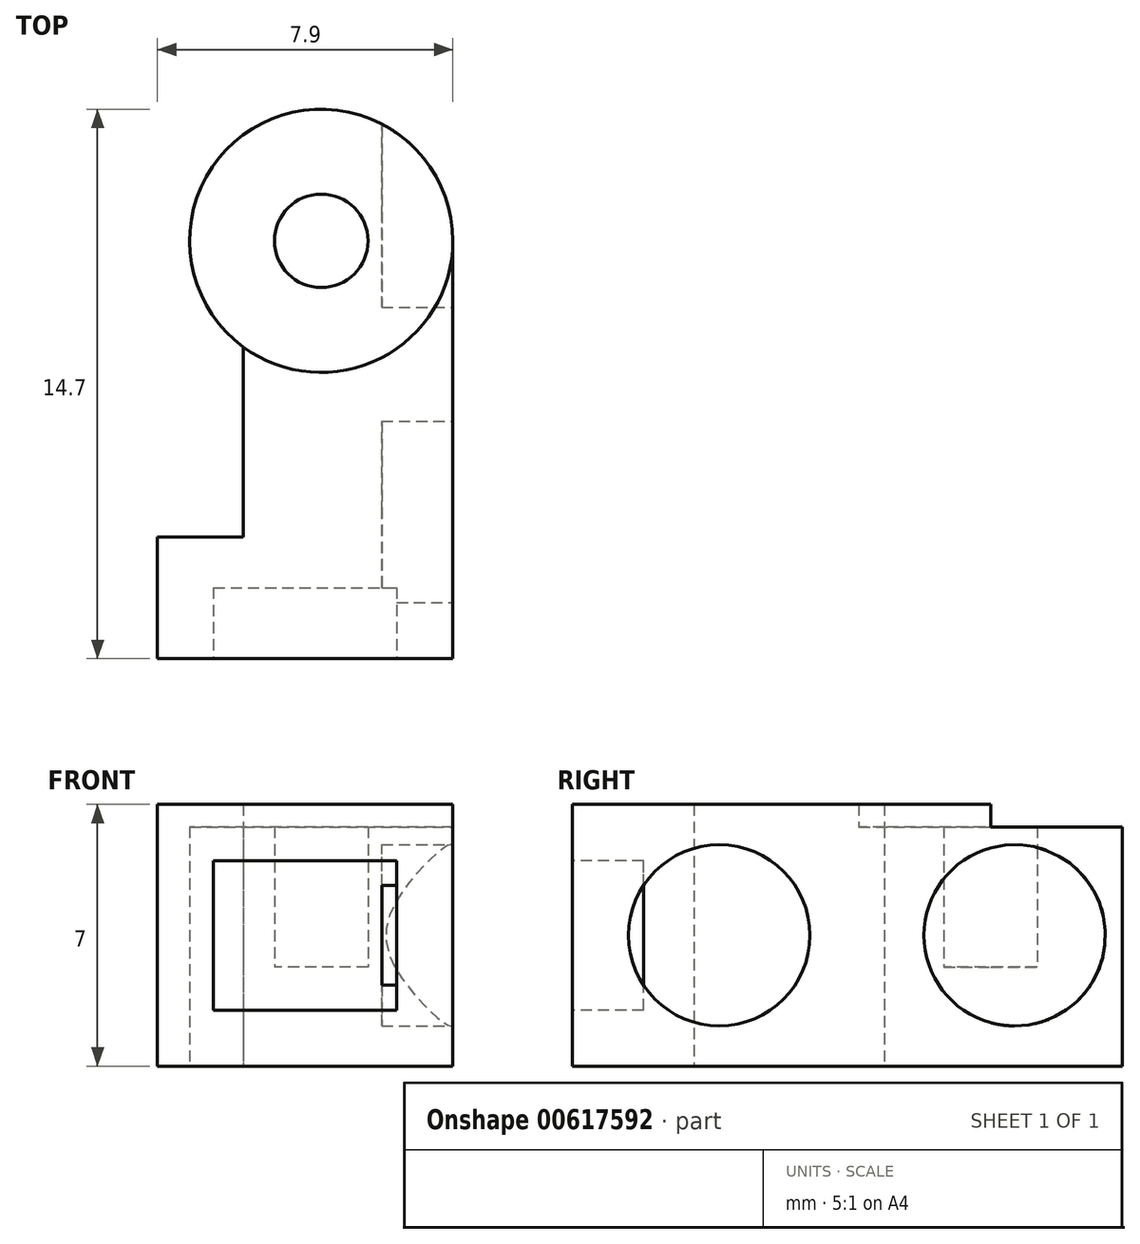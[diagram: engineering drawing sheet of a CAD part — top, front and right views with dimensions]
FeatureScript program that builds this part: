
annotation { "Feature Type Name" : "Feature", "Feature Type Description" : "" }
export const myFeature = defineFeature(function(context is Context, id is Id, definition is map)
    precondition{}
    {
        {
            var Q0;
            Q0=qCreatedBy(makeId("Top.planeOp"),FACE);
            var sketch = newSketch(context, id + "F0", { "sketchPlane" : qUnion([Q0])});
            skCircle(sketch, "E0", {"center": v(0, 0) * mm, "radius": 3.52 * mm});
            skLineSegment(sketch, "E1", {"start": v(0, 3.52) * mm, "end": v(0, -11.18) * mm, "construction": true});
            skLineSegment(sketch, "E2", {"start": v(0, -11.18) * mm, "end": v(3.52, -11.18) * mm});
            skLineSegment(sketch, "E3", {"start": v(3.52, -11.18) * mm, "end": v(3.52, 0) * mm});
            skLineSegment(sketch, "E4", {"start": v(0, -11.18) * mm, "end": v(-4.38, -11.18) * mm});
            skLineSegment(sketch, "E5", {"start": v(-4.38, -11.18) * mm, "end": v(-4.38, -7.93) * mm});
            skLineSegment(sketch, "E6", {"start": v(-4.38, -7.93) * mm, "end": v(-2.08, -7.93) * mm});
            skLineSegment(sketch, "E7", {"start": v(-2.08, -7.93) * mm, "end": v(-2.08, -2.84) * mm});
            skCircle(sketch, "E8", {"center": v(0, 0) * mm, "radius": 1.25 * mm});
            skSolve(sketch);
        }
        {
            var Q0;
            Q0=makeQuery(id+"F0.imprint","IMPRINT",FACE,{"disambiguationData":[TD([[makeQuery(id+"F0.imprint","IMPRINT",EDGE,{"derivedFrom":sQuery(id+"F0.wireOp",EDGE,"E2")}),1.0]])]});
            extrude(context, id + "F1", {"entities" : qUnion([Q0]), "depth" : 7 * mm, "offsetDistance" : 25 * mm});
        }
        {
            var Q0;
            Q0=makeQuery(id+"F0.imprint","IMPRINT",FACE,{"disambiguationData":[TD([[makeQuery(id+"F0.imprint","IMPRINT",EDGE,{"derivedFrom":sQuery(id+"F0.wireOp",EDGE,"E8")}),-1.0]])]});
            extrude(context, id + "F2", {"entities" : qUnion([Q0]), "operationType" : NewBodyOperationType.ADD, "depth" : 6.4 * mm, "offsetDistance" : 25 * mm});
        }
        {
            var Q0;
            Q0=makeQuery(id+"F0.imprint","IMPRINT",FACE,{"disambiguationData":[TD([[makeQuery(id+"F0.imprint","IMPRINT",EDGE,{"derivedFrom":sQuery(id+"F0.wireOp",EDGE,"E8")}),1.0]])]});
            extrude(context, id + "F3", {"entities" : qUnion([Q0]), "operationType" : NewBodyOperationType.ADD, "depth" : 2.65 * mm, "offsetDistance" : 25 * mm});
        }
        {
            var Q0;
            Q0=makeQuery(id+"F1.opExtrude","SWEPT_FACE",FACE,{"disambiguationData":[OSD([sQuery(id+"F0.wireOp",EDGE,"E2"),sQuery(id+"F0.wireOp",EDGE,"E4")])]});
            var sketch = newSketch(context, id + "F4", { "sketchPlane" : qUnion([Q0])});
            skLineSegment(sketch, "E9.bottom", {"start": v(-4.38, 0) * mm, "end": v(3.52, 0) * mm});
            skLineSegment(sketch, "E9.top", {"start": v(-4.38, 7) * mm, "end": v(3.52, 7) * mm});
            skLineSegment(sketch, "E9.left", {"start": v(-4.38, 0) * mm, "end": v(-4.38, 7) * mm});
            skLineSegment(sketch, "E9.right", {"start": v(3.52, 0) * mm, "end": v(3.52, 7) * mm});
            skLineSegment(sketch, "E10.0", {"start": v(-2.88, 1.5) * mm, "end": v(-2.88, 5.5) * mm});
            skLineSegment(sketch, "E10.1", {"start": v(-2.88, 1.5) * mm, "end": v(2.02, 1.5) * mm});
            skLineSegment(sketch, "E10.2", {"start": v(2.02, 1.5) * mm, "end": v(2.02, 5.5) * mm});
            skLineSegment(sketch, "E10.3", {"start": v(-2.88, 5.5) * mm, "end": v(2.02, 5.5) * mm});
            skSolve(sketch);
        }
        {
            var Q0;
            Q0=makeQuery(id+"F4.imprint","IMPRINT",FACE,{"disambiguationData":[TD([[makeQuery(id+"F4.imprint","IMPRINT",EDGE,{"derivedFrom":sQuery(id+"F4.wireOp",EDGE,"E10.0")}),-1.0]])]});
            extrude(context, id + "F5", {"entities" : qUnion([Q0]), "operationType" : NewBodyOperationType.REMOVE, "oppositeDirection" : true, "depth" : 1.9 * mm, "offsetDistance" : 25 * mm});
        }
        {
            var Q0;
            Q0=makeQuery(id+"F1.opExtrude","SWEPT_FACE",FACE,{"disambiguationData":[OSD([sQuery(id+"F0.wireOp",EDGE,"E3")])]});
            var sketch = newSketch(context, id + "F6", { "sketchPlane" : qUnion([Q0])});
            skLineSegment(sketch, "E11.bottom", {"start": v(-11.18, 0) * mm, "end": v(3.52, 0) * mm});
            skLineSegment(sketch, "E11.top", {"start": v(-11.18, 7) * mm, "end": v(3.52, 7) * mm});
            skLineSegment(sketch, "E11.left", {"start": v(-11.18, 0) * mm, "end": v(-11.18, 7) * mm});
            skLineSegment(sketch, "E11.right", {"start": v(3.52, 0) * mm, "end": v(3.52, 7) * mm});
            skLineSegment(sketch, "E12", {"start": v(-11.18, 3.5) * mm, "end": v(3.52, 3.5) * mm, "construction": true});
            skCircle(sketch, "E13", {"center": v(-7.25, 3.5) * mm, "radius": 2.43 * mm});
            skCircle(sketch, "E14", {"center": v(0.65, 3.5) * mm, "radius": 2.43 * mm});
            skSolve(sketch);
        }
        {
            var Q0;
            Q0=makeQuery(id+"F6.imprint","IMPRINT",FACE,{"disambiguationData":[TD([[makeQuery(id+"F6.imprint","IMPRINT",EDGE,{"derivedFrom":sQuery(id+"F6.wireOp",EDGE,"E13")}),1.0]])]});
            var Q1;
            {var subQ0=sQuery(id+"F6.wireOp",EDGE,"E14");var subQ1=sQuery(id+"F0.wireOp",EDGE,"E3");var subQ2=sQuery(id+"F0.wireOp",EDGE,"E0");var subQ3=makeQuery(id+"F2.boolean.opBoolean","SPLIT",EDGE,{"disambiguationData":[topologyDisambiguationEdgeConnected([makeQuery(id+"F2.opExtrude","SWEPT_FACE",FACE,{"disambiguationData":[OSD([subQ2])]})])],"derivedFrom":makeQuery(id+"F1.opExtrude","SWEPT_EDGE",EDGE,{"disambiguationData":[OSD([subQ2,subQ1])]})});var subQ4=makeQuery(id+"F6.imprint","INTERSECT",VERTEX,{"disambiguationData":[OD(0.0)],"derivedFrom":[subQ3,subQ0]});Q1=makeQuery(id+"F6.imprint","IMPRINT",FACE,{"disambiguationData":[TD([[makeQuery(id+"F6.imprint","IMPRINT",EDGE,{"disambiguationData":[TD([[subQ4,1.0]])],"derivedFrom":subQ0}),1.0]])]});}
            var Q2;
            {var subQ0=sQuery(id+"F6.wireOp",EDGE,"E14");var subQ1=sQuery(id+"F0.wireOp",EDGE,"E3");var subQ2=sQuery(id+"F0.wireOp",EDGE,"E0");var subQ3=makeQuery(id+"F2.boolean.opBoolean","SPLIT",EDGE,{"disambiguationData":[topologyDisambiguationEdgeConnected([makeQuery(id+"F2.opExtrude","SWEPT_FACE",FACE,{"disambiguationData":[OSD([subQ2])]})])],"derivedFrom":makeQuery(id+"F1.opExtrude","SWEPT_EDGE",EDGE,{"disambiguationData":[OSD([subQ2,subQ1])]})});var subQ4=makeQuery(id+"F6.imprint","INTERSECT",VERTEX,{"disambiguationData":[OD(0.0)],"derivedFrom":[subQ3,subQ0]});Q2=makeQuery(id+"F6.imprint","IMPRINT",FACE,{"disambiguationData":[TD([[makeQuery(id+"F6.imprint","IMPRINT",EDGE,{"disambiguationData":[TD([[subQ4,-1.0]])],"derivedFrom":subQ0}),1.0]])]});}
            extrude(context, id + "F7", {"entities" : qUnion([Q0, Q1, Q2]), "operationType" : NewBodyOperationType.REMOVE, "oppositeDirection" : true, "depth" : 1.9 * mm, "offsetDistance" : 25 * mm});
        }
    });
